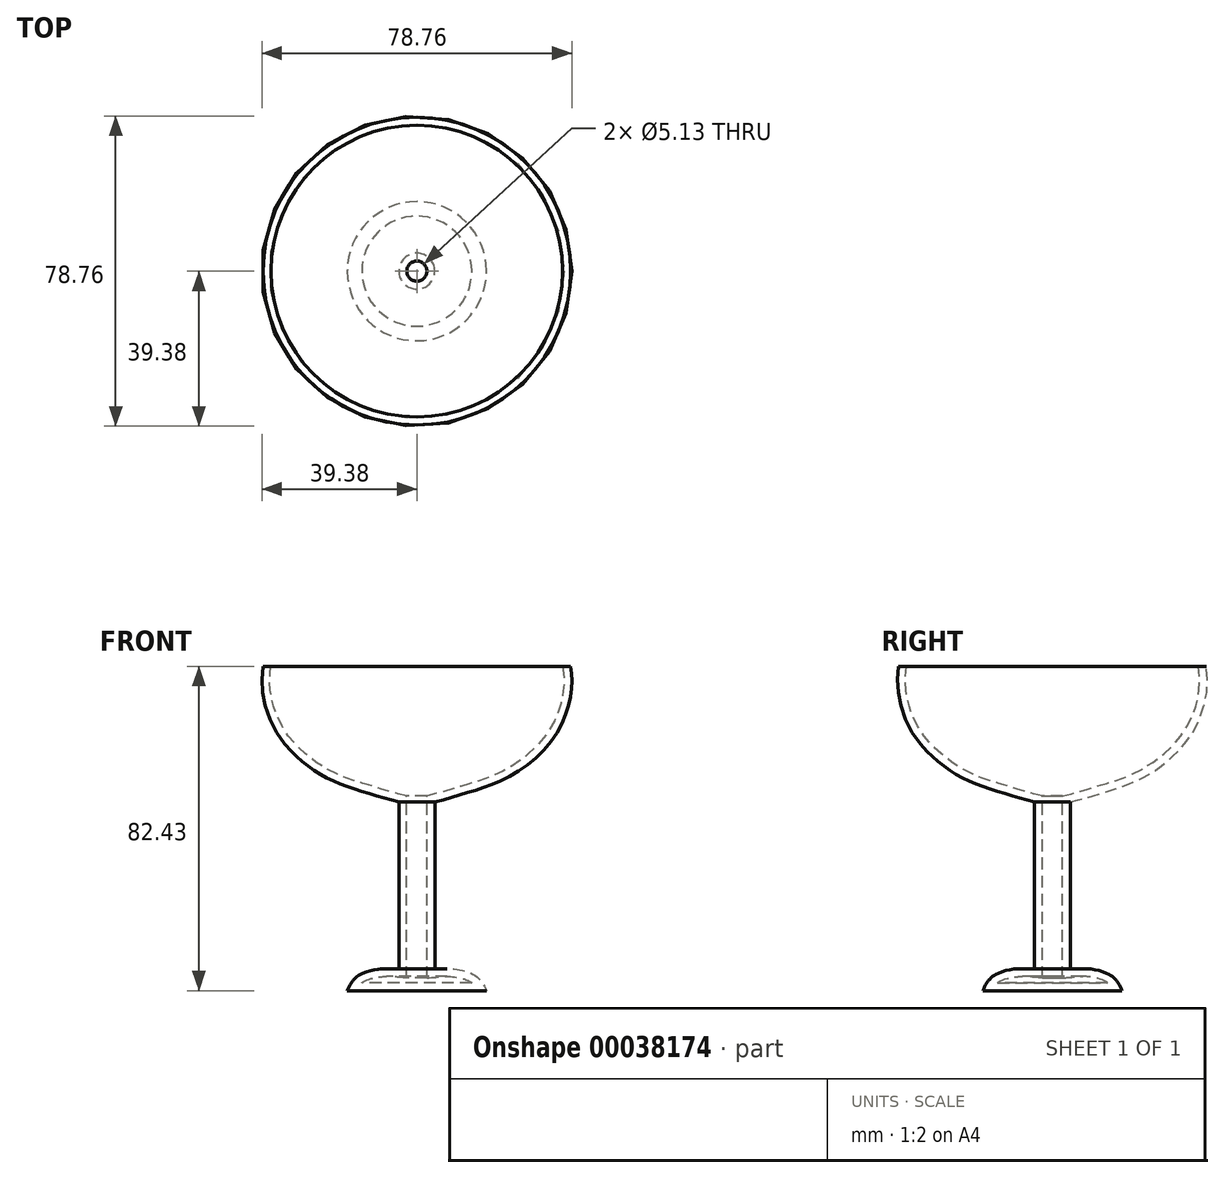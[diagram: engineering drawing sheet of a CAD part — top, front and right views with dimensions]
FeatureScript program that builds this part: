
annotation { "Feature Type Name" : "Feature", "Feature Type Description" : "" }
export const myFeature = defineFeature(function(context is Context, id is Id, definition is map)
    precondition{}
    {
        {
            var Q0;
            Q0=qCreatedBy(makeId("Front.planeOp"),FACE);
            var sketch = newSketch(context, id + "F0", { "sketchPlane" : qUnion([Q0])});
            skLineSegment(sketch, "E0", {"start": v(0, 38.65) * mm, "end": v(0, -43.78) * mm});
            skLineSegment(sketch, "E1", {"start": v(0, 38.65) * mm, "end": v(39.08, 38.65) * mm});
            skLineSegment(sketch, "E2", {"start": v(0, -43.78) * mm, "end": v(17.68, -43.78) * mm});
            skLineSegment(sketch, "E3", {"start": v(4.56, 4.14) * mm, "end": v(4.56, -38.36) * mm});
            skFitSpline(sketch, "E4", {"points": [v(39.08, 38.65) * mm, v(39.08, 31.23) * mm, v(34.52, 20.1) * mm, v(23.1, 10.41) * mm, v(13.4, 6.7) * mm, v(4.56, 4.14) * mm], "startDerivative": vector(6.48, -43.44) * mm, "endDerivative": vector(-51.27, -13.11) * mm});
            skFitSpline(sketch, "E5", {"points": [v(4.56, -38.36) * mm, v(10.27, -38.36) * mm, v(15.4, -40.36) * mm, v(17.68, -43.78) * mm], "startDerivative": vector(16.35, 1.62) * mm, "endDerivative": vector(5.82, -12.96) * mm});
            skSolve(sketch);
        }
        {
            var Q0;
            Q0=makeQuery(id+"F0.imprint","IMPRINT",FACE,{"disambiguationData":[TD([[makeQuery(id+"F0.imprint","IMPRINT",EDGE,{"derivedFrom":sQuery(id+"F0.wireOp",EDGE,"E0")}),1.0]])]});
            var Q1;
            Q1=sQuery(id+"F0.wireOp",EDGE,"E0");
            revolve(context, id + "F1", {"entities" : qUnion([Q0]), "axis" : qUnion([Q1]), "revolveType" : RevolveType.FULL});
        }
        {
            var Q0;
            Q0=makeQuery(id+"F1.opRevolve","SWEPT_FACE",FACE,{"disambiguationData":[OSD([sQuery(id+"F0.wireOp",EDGE,"E1")])]});
            shell(context, id + "F2", {"entities" : qUnion([Q0]), "thickness" : 2 * mm});
        }
    });
